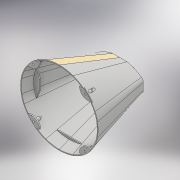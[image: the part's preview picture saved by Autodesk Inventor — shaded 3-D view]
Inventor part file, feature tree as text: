
AUTODESK INVENTOR PART (.ipt)
format: ipt  version: 2017 (Build 210142000, 142)  size: 1,990,144 bytes
history: native  units: mm
features: sketch x37, extrude x35, projected_geometry x7, plane x4, chamfer x2, fillet x1, loft x1, mirror x1, shell x1, other x1
ambient origin geometry x8: Origin, YZ Plane, XZ Plane, XY Plane, X Axis, Y Axis, Z Axis, Center Point
bodies: Solid1 (feature_tree)
feature tree (90):
  extrude  "Extrusion1"  Depth=35.0mm
  extrude  "Extrusion2"  Depth=9.0mm TaperAngle=0.0deg
  extrude  "Extrusion6"  Depth=70.0mm TaperAngle=0.0deg
  extrude  "Extrusion9"  Depth=10.0mm
  extrude  "Extrusion11"  Depth=200.0mm
  fillet  "Fillet2"  [1 undecoded]
  sketch  "Sketch29"  dims[d72=0.0mm d73=90.0deg d81=2.0mm d83=-324.476mm]
  plane  "Work Plane8"
  loft  "Loft1"
  mirror  "Mirror8"
  shell  "Shell3"  Thickness=-324.476mm
  plane  "Work Plane9"
  extrude  "Extrusion16"  [1 undecoded]
  plane  "Work Plane10"
  extrude  "Extrusion17"  Depth=1.5mm TaperAngle=0.0deg
  extrude  "Extrusion18"  Depth=3.0mm TaperAngle=0.0deg
  extrude  "Extrusion19"  Depth=173.3463mm TaperAngle=0.0deg
  extrude  "Extrusion20"  Depth=43.5mm
  extrude  "Extrusion21"  Depth=2.0mm
  extrude  "Extrusion22"  Depth=2.0mm
  extrude  "Extrusion23"  Depth=12.0mm
  extrude  "Extrusion24"  Depth=16.0mm
  extrude  "Extrusion25"  Depth=10.0mm TaperAngle=0.0deg
  extrude  "Extrusion26"  Depth=4.0mm
  extrude  "Extrusion27"  Depth=6.0mm
  extrude  "Extrusion28"  Depth=12.0mm
  extrude  "Extrusion29"  Depth=2.5mm
  extrude  "Extrusion30"  Depth=25.0mm TaperAngle=0.0deg
  extrude  "Extrusion31"  Depth=8.0mm
  extrude  "Extrusion32"  Depth=2.0mm
  extrude  "Extrusion33"  Depth=28.0mm
  extrude  "Extrusion34"  Depth=18.0mm
  extrude  "Extrusion38"  Depth=8.0mm TaperAngle=0.0deg
  extrude  "Extrusion39"  Depth=9.0mm
  extrude  "Extrusion40"  Depth=5.0mm
  extrude  "Extrusion41"  Depth=10.0mm
  extrude  "Extrusion42"  Depth=10.0mm TaperAngle=0.0deg
  extrude  "Extrusion43"  Depth=3.0mm
  chamfer  "Chamfer3"  Distance=6.0mm
  chamfer  "Chamfer4"  Distance=40.0mm
  extrude  "Extrusion44"  Depth=10.0mm
  extrude  "Extrusion45"  Depth=10.0mm
  extrude  "Extrusion46"  Depth=10.0mm
  plane  "Work Plane11"
  extrude  "Extrusion47"  Depth=10.0mm TaperAngle=0.0deg
  extrude  "Extrusion48"  Depth=10.0mm TaperAngle=0.0deg
  sketch  "Sketch1"  dims[d0=63.0mm d1=0.0mm d2=35.0mm]
  sketch  "Sketch3"  dims[d3=150.0mm d4=9.0mm d5=0.0mm]
  sketch  "Sketch12"  dims[d30=250.0mm d31=0.0mm d48=70.0mm d49=0.0mm]
  sketch  "Sketch17"  dims[d53=70.0mm d54=0.0mm d55=10.0mm]
  sketch  "Sketch20"  dims[d68=-347.0mm d69=200.0mm d70=0.0mm d71=90.0deg]
  projected_geometry  "Projected Loop9"
  sketch  "Sketch30"  dims[d93=2.5mm d94=0.0mm d96=-15.524mm]
  other  "Edges1"
  sketch  "Sketch37"  dims[d102=4.0mm d103=0.0mm d104=1.5mm d105=0.0mm]
  sketch  "Sketch38"  dims[d106=2.0mm d107=0.0mm d111=3.0mm d112=0.0mm]
  sketch  "Sketch39"  dims[d113=12.0mm d114=0.0mm d115=173.3463mm d116=0.0mm]
  projected_geometry  "Projected Loop13"
  projected_geometry  "Projected Loop14"
  sketch  "Sketch41"  dims[d117=6.25mm d118=43.5mm]
  sketch  "Sketch43"  dims[d119=43.5mm d129=2.0mm]
  sketch  "Sketch44"  dims[d130=2.0mm d131=2.0mm]
  projected_geometry  "Projected Loop15"
  projected_geometry  "Projected Loop16"
  sketch  "Sketch45"  dims[d132=3.0mm d133=0.0mm d134=12.0mm]
  sketch  "Sketch46"  dims[d135=24.0mm d136=16.0mm]
  sketch  "Sketch47"  dims[d137=16.0mm d138=10.0mm d139=0.0mm]
  sketch  "Sketch48"  dims[d140=4.0mm d141=4.0mm]
  sketch  "Sketch49"  dims[d142=30.0mm d143=0.0mm d144=6.0mm]
  sketch  "Sketch50"  dims[d145=6.0mm d146=12.0mm]
  sketch  "Sketch51"  dims[d147=2.0mm d148=0.0mm d152=2.5mm]
  sketch  "Sketch52"  dims[d153=2.5mm d154=25.0mm d155=0.0mm]
  sketch  "Sketch53"  dims[d156=3.0mm d157=8.0mm]
  sketch  "Sketch54"  dims[d158=40.0mm d159=0.0mm d160=2.0mm]
  sketch  "Sketch55"  dims[d161=18.0mm d162=28.0mm]
  sketch  "Sketch56"  dims[d163=2.0mm d164=18.0mm]
  sketch  "Sketch57"  dims[d165=28.0mm d166=8.0mm d167=0.0mm]
  sketch  "Sketch61"  dims[d168=9.0mm d169=9.0mm]
  sketch  "Sketch62"  dims[d170=2.0mm d171=0.0mm d172=5.0mm]
  projected_geometry  "Projected Loop17"
  sketch  "Sketch64"  dims[d173=10.0mm d174=3.0mm]
  sketch  "Sketch65"  dims[d176=10.0mm d178=6.0mm d179=0.0mm]
  sketch  "Sketch66"  dims[d181=60.0mm d182=0.0mm d183=3.0mm]
  sketch  "Sketch67"  dims[d184=3.0mm]
  sketch  "Sketch68"  dims[d185=3.0mm]
  sketch  "Sketch69"  dims[d186=3.0mm d187=6.0mm d188=0.0mm]
  sketch  "Sketch70"  dims[d189=3.0mm]
  projected_geometry  "Projected Loop18"
  sketch  "Sketch72"  dims[d190=40.0mm]
  sketch  "Sketch73"  dims[d191=3.0mm d192=40.0mm d193=3.0mm d194=40.0mm d195=3.0mm d196=10.0mm d197=0.0mm d204=28.654mm d205=0.0mm d206=30.0mm d207=0.0mm d209=3.0mm d210=0.0mm d211=30.0mm d212=0.0mm d213=8.0mm d214=8.0mm d215=8.0mm d216=8.0mm d217=6.0mm d218=6.0mm d219=6.0mm d220=6.0mm d221=10.0mm d222=0.0mm d223=6.0mm d224=6.0mm d225=6.0mm d226=6.0mm d227=25.0mm d228=0.0mm d229=0.9mm d230=2.0mm d231=45.0deg d232=1.2mm d233=2.0mm d234=45.0deg d236=8.0mm d238=8.0mm d239=2.0mm d240=0.0mm d241=45.0deg d242=135.0deg d243=45.0deg d244=135.0deg d245=2.0mm d246=0.0mm d247=3.0mm d248=3.0mm d249=3.0mm d250=3.0mm d251=2.0mm d252=0.0mm d253=-295.0mm d255=2.5mm d256=0.0mm d257=2.5mm d258=0.0mm]
note: 2 required parameter values undecoded (feature->parameter linkage not recoverable at this tier; creation-order binding heuristic only, values carry confidence <= 0.55)
